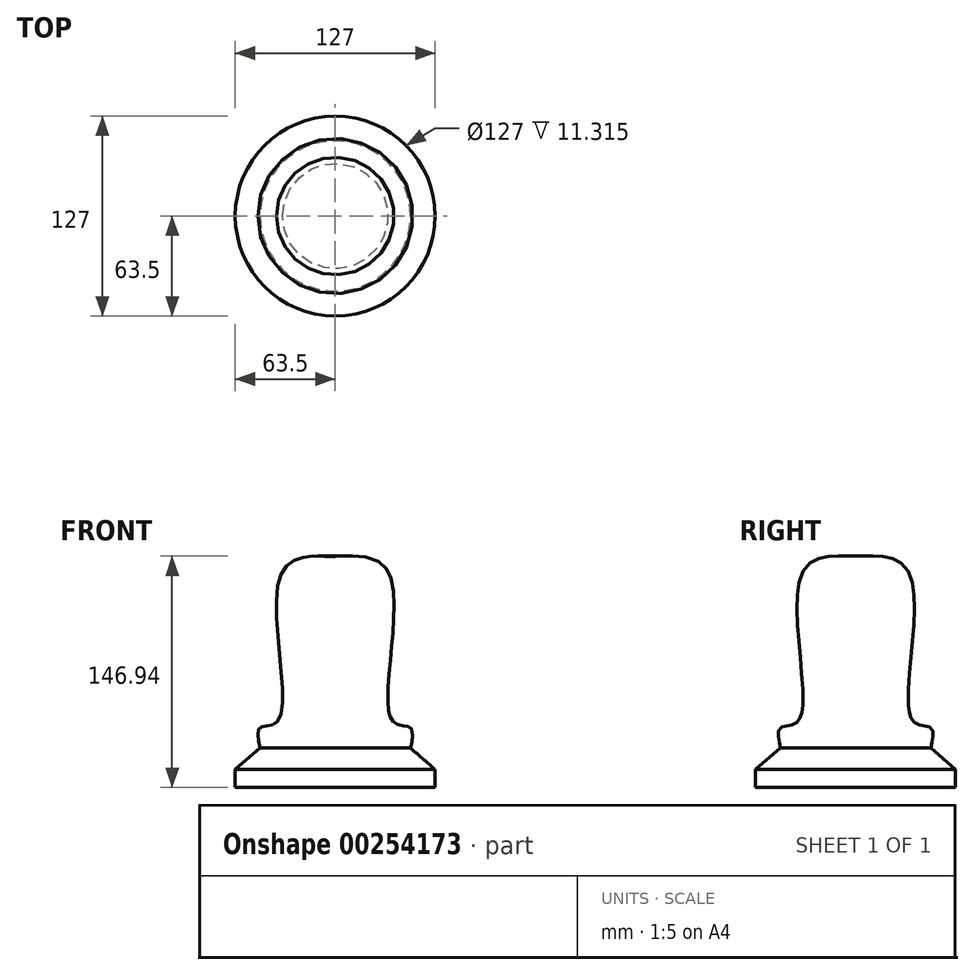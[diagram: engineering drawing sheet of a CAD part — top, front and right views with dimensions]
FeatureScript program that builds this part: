
annotation { "Feature Type Name" : "Feature", "Feature Type Description" : "" }
export const myFeature = defineFeature(function(context is Context, id is Id, definition is map)
    precondition{}
    {
        {
            var Q0;
            Q0=qCreatedBy(makeId("Front.planeOp"),FACE);
            var sketch = newSketch(context, id + "F0", { "sketchPlane" : qUnion([Q0])});
            skLineSegment(sketch, "E0", {"start": v(0, -92.55) * mm, "end": v(0, 116.85) * mm, "construction": true});
            skLineSegment(sketch, "E1", {"start": v(0, -92.55) * mm, "end": v(-63.5, -92.55) * mm});
            skLineSegment(sketch, "E2", {"start": v(-63.5, -92.55) * mm, "end": v(-63.5, -81.23) * mm});
            skLineSegment(sketch, "E3", {"start": v(-63.5, -81.23) * mm, "end": v(-47.72, -67.48) * mm});
            skFitSpline(sketch, "E4", {"points": [v(-47.72, -67.48) * mm, v(-47.72, -54.51) * mm, v(-35.93, -49.8) * mm, v(-34.75, 42.14) * mm, v(0, 53.93) * mm], "startDerivative": vector(-24.17, 105.35) * mm, "endDerivative": vector(166.43, -10.4) * mm});
            skSolve(sketch);
        }
        {
            var Q0;
            Q0=sQuery(id+"F0.wireOp",EDGE,"E4");
            var Q1;
            Q1=sQuery(id+"F0.wireOp",EDGE,"E3");
            var Q2;
            Q2=sQuery(id+"F0.wireOp",EDGE,"E1");
            var Q3;
            Q3=sQuery(id+"F0.wireOp",EDGE,"E2");
            var Q4;
            Q4=sQuery(id+"F0.wireOp",EDGE,"E0");
            revolve(context, id + "F1", {"bodyType" : ToolBodyType.SURFACE, "surfaceEntities" : qUnion([Q0, Q1, Q2, Q3]), "axis" : qUnion([Q4]), "revolveType" : RevolveType.FULL});
        }
    });
